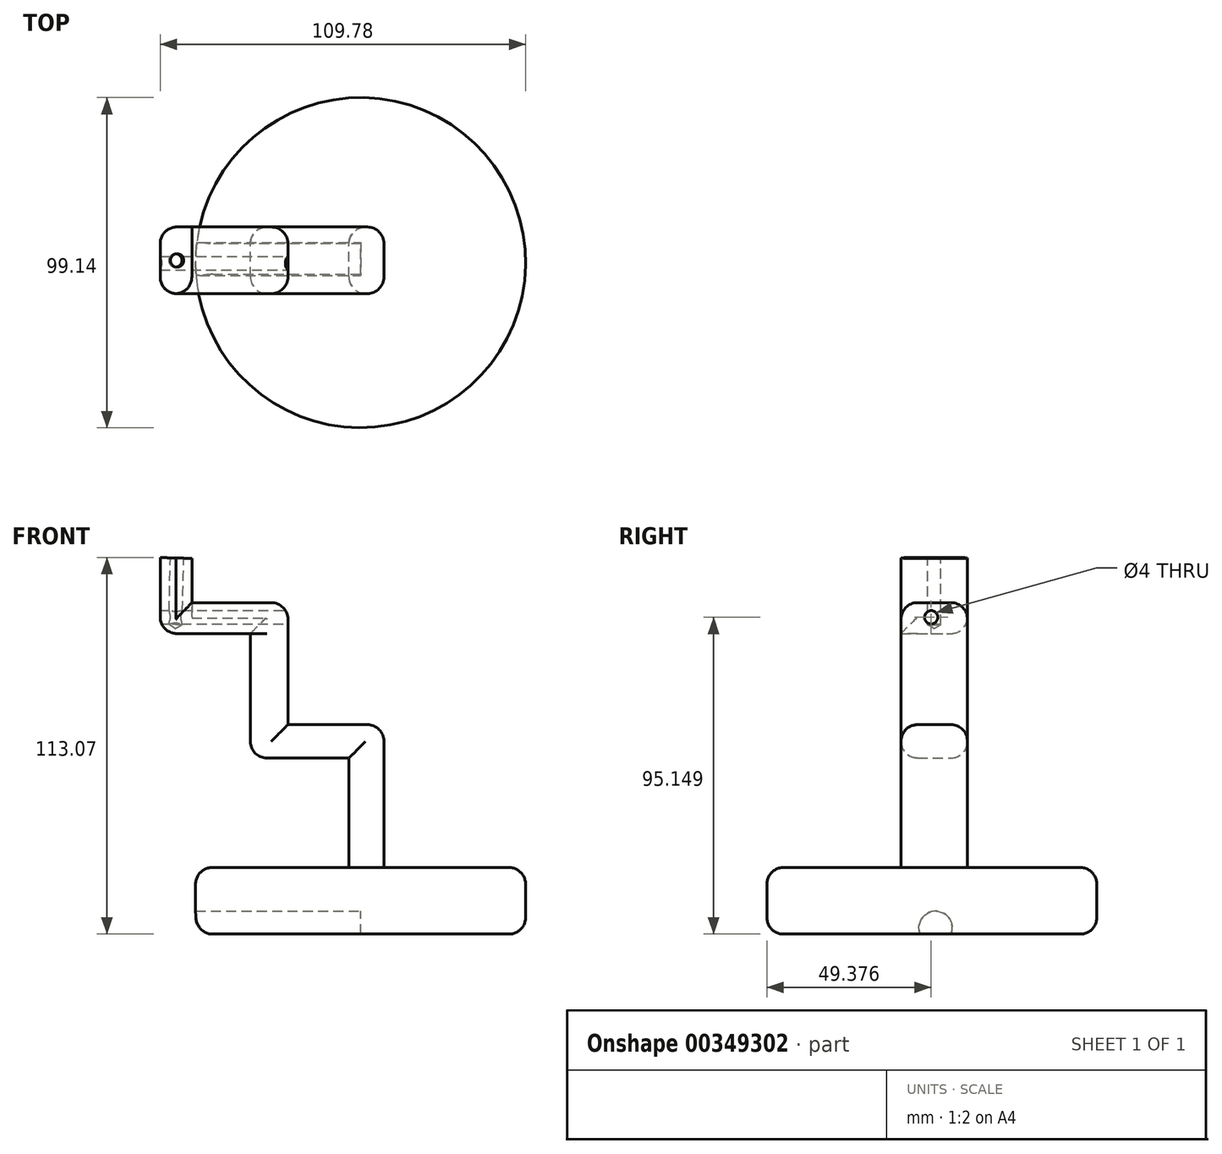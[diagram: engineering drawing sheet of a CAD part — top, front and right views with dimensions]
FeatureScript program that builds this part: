
annotation { "Feature Type Name" : "Feature", "Feature Type Description" : "" }
export const myFeature = defineFeature(function(context is Context, id is Id, definition is map)
    precondition{}
    {
        {
            var Q0;
            Q0=qCreatedBy(makeId("Front.planeOp"),FACE);
            var sketch = newSketch(context, id + "F0", { "sketchPlane" : qUnion([Q0])});
            skLineSegment(sketch, "E0", {"start": v(-60.21, 43.65) * mm, "end": v(-60.21, 20.82) * mm});
            skLineSegment(sketch, "E1", {"start": v(-60.21, 20.82) * mm, "end": v(-33.12, 20.82) * mm});
            skLineSegment(sketch, "E2", {"start": v(-33.12, 20.82) * mm, "end": v(-33.12, -16.56) * mm});
            skLineSegment(sketch, "E3", {"start": v(-33.12, -16.56) * mm, "end": v(-3.51, -16.56) * mm});
            skLineSegment(sketch, "E4", {"start": v(-3.51, -16.56) * mm, "end": v(-3.51, -49.42) * mm});
            skLineSegment(sketch, "E5", {"start": v(-3.51, -49.42) * mm, "end": v(7.02, -49.42) * mm});
            skLineSegment(sketch, "E6", {"start": v(7.02, -49.42) * mm, "end": v(7.02, -6.52) * mm});
            skLineSegment(sketch, "E7", {"start": v(7.02, -6.52) * mm, "end": v(-21.83, -6.52) * mm});
            skLineSegment(sketch, "E8", {"start": v(-21.83, -6.52) * mm, "end": v(-21.83, 30.1) * mm});
            skLineSegment(sketch, "E9", {"start": v(-21.83, 30.1) * mm, "end": v(-50.68, 30.1) * mm});
            skLineSegment(sketch, "E10", {"start": v(-50.68, 30.1) * mm, "end": v(-50.68, 43.4) * mm});
            skLineSegment(sketch, "E11", {"start": v(-50.68, 43.4) * mm, "end": v(-60.21, 43.65) * mm});
            skSolve(sketch);
        }
        {
            var Q0;
            Q0=makeQuery(id+"F0.imprint","IMPRINT",FACE,{"disambiguationData":[TD([[makeQuery(id+"F0.imprint","IMPRINT",EDGE,{"derivedFrom":sQuery(id+"F0.wireOp",EDGE,"E0")}),1.0]])]});
            extrude(context, id + "F1", {"entities" : qUnion([Q0]), "depth" : 20 * mm});
        }
        {
            var Q0;
            Q0=makeQuery(id+"F1.opExtrude","SWEPT_FACE",FACE,{"disambiguationData":[OSD([sQuery(id+"F0.wireOp",EDGE,"E5")])]});
            var sketch = newSketch(context, id + "F2", { "sketchPlane" : qUnion([Q0])});
            skCircle(sketch, "E12", {"center": v(0, 10.7) * mm, "radius": 49.57 * mm});
            skSolve(sketch);
        }
        {
            var Q0;
            Q0 = qSketchRegion(id + "F2", true);
            extrude(context, id + "F3", {"entities" : qUnion([Q0]), "operationType" : NewBodyOperationType.ADD, "depth" : 20 * mm});
        }
        {
            var Q0;
            Q0=makeQuery(id+"F1.opExtrude","SWEPT_FACE",FACE,{"disambiguationData":[OSD([sQuery(id+"F0.wireOp",EDGE,"E11")])]});
            var sketch = newSketch(context, id + "F4", { "sketchPlane" : qUnion([Q0])});
            skCircle(sketch, "E13", {"center": v(-56.24, -10.04) * mm, "radius": 2.38 * mm});
            skSolve(sketch);
        }
        {
            var Q0;
            Q0=sQuery(id+"F4.wireOp",VERTEX,"E13.center");
            var Q1;
            Q1=makeQuery(id+"F1.opExtrude","SWEPT_BODY",BODY,{"disambiguationData":[OSD([sQuery(id+"F0.wireOp",EDGE,"E0"),sQuery(id+"F0.wireOp",EDGE,"E1"),sQuery(id+"F0.wireOp",EDGE,"E2"),sQuery(id+"F0.wireOp",EDGE,"E3"),sQuery(id+"F0.wireOp",EDGE,"E4"),sQuery(id+"F0.wireOp",EDGE,"E5"),sQuery(id+"F0.wireOp",EDGE,"E6"),sQuery(id+"F0.wireOp",EDGE,"E7"),sQuery(id+"F0.wireOp",EDGE,"E8"),sQuery(id+"F0.wireOp",EDGE,"E9"),sQuery(id+"F0.wireOp",EDGE,"E10"),sQuery(id+"F0.wireOp",EDGE,"E11")])]});
            hole(context, id + "F5", {"style" : HoleStyle.SIMPLE, "endStyle" : HoleEndStyle.BLIND, "holeDiameter" : 4 * mm, "holeDepth" : 20 * mm, "isTappedThrough" : true, "tappedDepth" : 12 * mm, "tapClearance" : 3, "locations" : qUnion([Q0]), "scope" : qUnion([Q1])});
        }
        {
            var Q0;
            Q0=makeQuery(id+"F1.opExtrude","SWEPT_FACE",FACE,{"disambiguationData":[OSD([sQuery(id+"F0.wireOp",EDGE,"E8")])]});
            var sketch = newSketch(context, id + "F6", { "sketchPlane" : qUnion([Q0])});
            skCircle(sketch, "E14", {"center": v(-10.9, 25.73) * mm, "radius": 1.88 * mm});
            skSolve(sketch);
        }
        {
            var Q0;
            Q0=sQuery(id+"F6.wireOp",VERTEX,"E14.center");
            var Q1;
            Q1=makeQuery(id+"F1.opExtrude","SWEPT_BODY",BODY,{"disambiguationData":[OSD([sQuery(id+"F0.wireOp",EDGE,"E0"),sQuery(id+"F0.wireOp",EDGE,"E1"),sQuery(id+"F0.wireOp",EDGE,"E2"),sQuery(id+"F0.wireOp",EDGE,"E3"),sQuery(id+"F0.wireOp",EDGE,"E4"),sQuery(id+"F0.wireOp",EDGE,"E5"),sQuery(id+"F0.wireOp",EDGE,"E6"),sQuery(id+"F0.wireOp",EDGE,"E7"),sQuery(id+"F0.wireOp",EDGE,"E8"),sQuery(id+"F0.wireOp",EDGE,"E9"),sQuery(id+"F0.wireOp",EDGE,"E10"),sQuery(id+"F0.wireOp",EDGE,"E11")])]});
            hole(context, id + "F7", {"style" : HoleStyle.SIMPLE, "endStyle" : HoleEndStyle.THROUGH, "holeDiameter" : 4 * mm, "isTappedThrough" : true, "tappedDepth" : 12 * mm, "tapClearance" : 3, "locations" : qUnion([Q0]), "scope" : qUnion([Q1])});
        }
        {
            var Q0;
            Q0=qCreatedBy(makeId("Right.planeOp"),FACE);
            var sketch = newSketch(context, id + "F8", { "sketchPlane" : qUnion([Q0])});
            skCircle(sketch, "E15", {"center": v(-9.6, -67.53) * mm, "radius": 3.5 * mm});
            skSolve(sketch);
        }
        {
            var Q0;
            Q0=sQuery(id+"F8.wireOp",VERTEX,"E15.center");
            var Q1;
            Q1=makeQuery(id+"F1.opExtrude","SWEPT_BODY",BODY,{"disambiguationData":[OSD([sQuery(id+"F0.wireOp",EDGE,"E0"),sQuery(id+"F0.wireOp",EDGE,"E1"),sQuery(id+"F0.wireOp",EDGE,"E2"),sQuery(id+"F0.wireOp",EDGE,"E3"),sQuery(id+"F0.wireOp",EDGE,"E4"),sQuery(id+"F0.wireOp",EDGE,"E5"),sQuery(id+"F0.wireOp",EDGE,"E6"),sQuery(id+"F0.wireOp",EDGE,"E7"),sQuery(id+"F0.wireOp",EDGE,"E8"),sQuery(id+"F0.wireOp",EDGE,"E9"),sQuery(id+"F0.wireOp",EDGE,"E10"),sQuery(id+"F0.wireOp",EDGE,"E11")])]});
            hole(context, id + "F9", {"style" : HoleStyle.SIMPLE, "endStyle" : HoleEndStyle.THROUGH, "holeDiameter" : 10 * mm, "isTappedThrough" : true, "tappedDepth" : 12 * mm, "tapClearance" : 3, "locations" : qUnion([Q0]), "scope" : qUnion([Q1])});
        }
        {
            var Q0;
            Q0=makeQuery(id+"F1.opExtrude","CAP_EDGE",EDGE,{"disambiguationData":[OSD([sQuery(id+"F0.wireOp",EDGE,"E9")])],"isStart":false});
            var Q1;
            Q1=makeQuery(id+"F1.opExtrude","CAP_EDGE",EDGE,{"disambiguationData":[OSD([sQuery(id+"F0.wireOp",EDGE,"E10")])],"isStart":false});
            fillet(context, id + "F10", {"entities" : qUnion([Q0, Q1]), "radius" : 5 * mm, "tangentPropagation" : true, "allowEdgeOverflow" : false});
        }
        {
            var Q0;
            Q0=makeQuery(id+"F1.opExtrude","CAP_EDGE",EDGE,{"disambiguationData":[OSD([sQuery(id+"F0.wireOp",EDGE,"E0")])],"isStart":false});
            fillet(context, id + "F11", {"entities" : qUnion([Q0]), "radius" : 5 * mm, "tangentPropagation" : true, "allowEdgeOverflow" : false});
        }
        {
            var Q0;
            Q0=makeQuery(id+"F1.opExtrude","CAP_EDGE",EDGE,{"disambiguationData":[OSD([sQuery(id+"F0.wireOp",EDGE,"E1")])],"isStart":false});
            fillet(context, id + "F12", {"entities" : qUnion([Q0]), "radius" : 5 * mm, "tangentPropagation" : true, "allowEdgeOverflow" : false});
        }
        {
            var Q0;
            Q0=makeQuery(id+"F1.opExtrude","CAP_EDGE",EDGE,{"disambiguationData":[OSD([sQuery(id+"F0.wireOp",EDGE,"E0")])],"isStart":true});
            fillet(context, id + "F13", {"entities" : qUnion([Q0]), "radius" : 5 * mm, "tangentPropagation" : true, "allowEdgeOverflow" : false});
        }
        {
            var Q0;
            Q0=makeQuery(id+"F1.opExtrude","CAP_EDGE",EDGE,{"disambiguationData":[OSD([sQuery(id+"F0.wireOp",EDGE,"E2")])],"isStart":true});
            fillet(context, id + "F14", {"entities" : qUnion([Q0]), "radius" : 5 * mm, "tangentPropagation" : true, "allowEdgeOverflow" : false});
        }
        {
            var Q0;
            Q0=makeQuery(id+"F1.opExtrude","CAP_EDGE",EDGE,{"disambiguationData":[OSD([sQuery(id+"F0.wireOp",EDGE,"E3")])],"isStart":true});
            var Q1;
            Q1=makeQuery(id+"F1.opExtrude","CAP_EDGE",EDGE,{"disambiguationData":[OSD([sQuery(id+"F0.wireOp",EDGE,"E4")])],"isStart":true});
            var Q2;
            Q2=makeQuery(id+"F1.opExtrude","CAP_EDGE",EDGE,{"disambiguationData":[OSD([sQuery(id+"F0.wireOp",EDGE,"E6")])],"isStart":true});
            var Q3;
            Q3=makeQuery(id+"F1.opExtrude","CAP_EDGE",EDGE,{"disambiguationData":[OSD([sQuery(id+"F0.wireOp",EDGE,"E6")])],"isStart":false});
            var Q4;
            Q4=makeQuery(id+"F1.opExtrude","CAP_EDGE",EDGE,{"disambiguationData":[OSD([sQuery(id+"F0.wireOp",EDGE,"E4")])],"isStart":false});
            var Q5;
            Q5=makeQuery(id+"F1.opExtrude","CAP_EDGE",EDGE,{"disambiguationData":[OSD([sQuery(id+"F0.wireOp",EDGE,"E3")])],"isStart":false});
            var Q6;
            Q6=makeQuery(id+"F1.opExtrude","CAP_EDGE",EDGE,{"disambiguationData":[OSD([sQuery(id+"F0.wireOp",EDGE,"E2")])],"isStart":false});
            var Q7;
            Q7=makeQuery(id+"F1.opExtrude","CAP_EDGE",EDGE,{"disambiguationData":[OSD([sQuery(id+"F0.wireOp",EDGE,"E7")])],"isStart":false});
            var Q8;
            Q8=makeQuery(id+"F1.opExtrude","CAP_EDGE",EDGE,{"disambiguationData":[OSD([sQuery(id+"F0.wireOp",EDGE,"E8")])],"isStart":false});
            var Q9;
            Q9=makeQuery(id+"F1.opExtrude","CAP_EDGE",EDGE,{"disambiguationData":[OSD([sQuery(id+"F0.wireOp",EDGE,"E7")])],"isStart":true});
            var Q10;
            Q10=makeQuery(id+"F1.opExtrude","CAP_EDGE",EDGE,{"disambiguationData":[OSD([sQuery(id+"F0.wireOp",EDGE,"E8")])],"isStart":true});
            var Q11;
            Q11=makeQuery(id+"F1.opExtrude","CAP_EDGE",EDGE,{"disambiguationData":[OSD([sQuery(id+"F0.wireOp",EDGE,"E9")])],"isStart":true});
            var Q12;
            Q12=makeQuery(id+"F1.opExtrude","SWEPT_EDGE",EDGE,{"disambiguationData":[OSD([sQuery(id+"F0.wireOp",EDGE,"E6"),sQuery(id+"F0.wireOp",EDGE,"E7")])]});
            var Q13;
            Q13=makeQuery(id+"F3.opExtrude","CAP_EDGE",EDGE,{"disambiguationData":[OSD([sQuery(id+"F2.wireOp",EDGE,"E12")])],"isStart":true});
            var Q14;
            Q14=makeQuery(id+"F3.opExtrude","CAP_EDGE",EDGE,{"disambiguationData":[OSD([sQuery(id+"F2.wireOp",EDGE,"E12")])],"isStart":false});
            fillet(context, id + "F15", {"entities" : qUnion([Q0, Q1, Q2, Q3, Q4, Q5, Q6, Q7, Q8, Q9, Q10, Q11, Q12, Q13, Q14]), "radius" : 5 * mm, "tangentPropagation" : true, "allowEdgeOverflow" : false});
        }
    });
